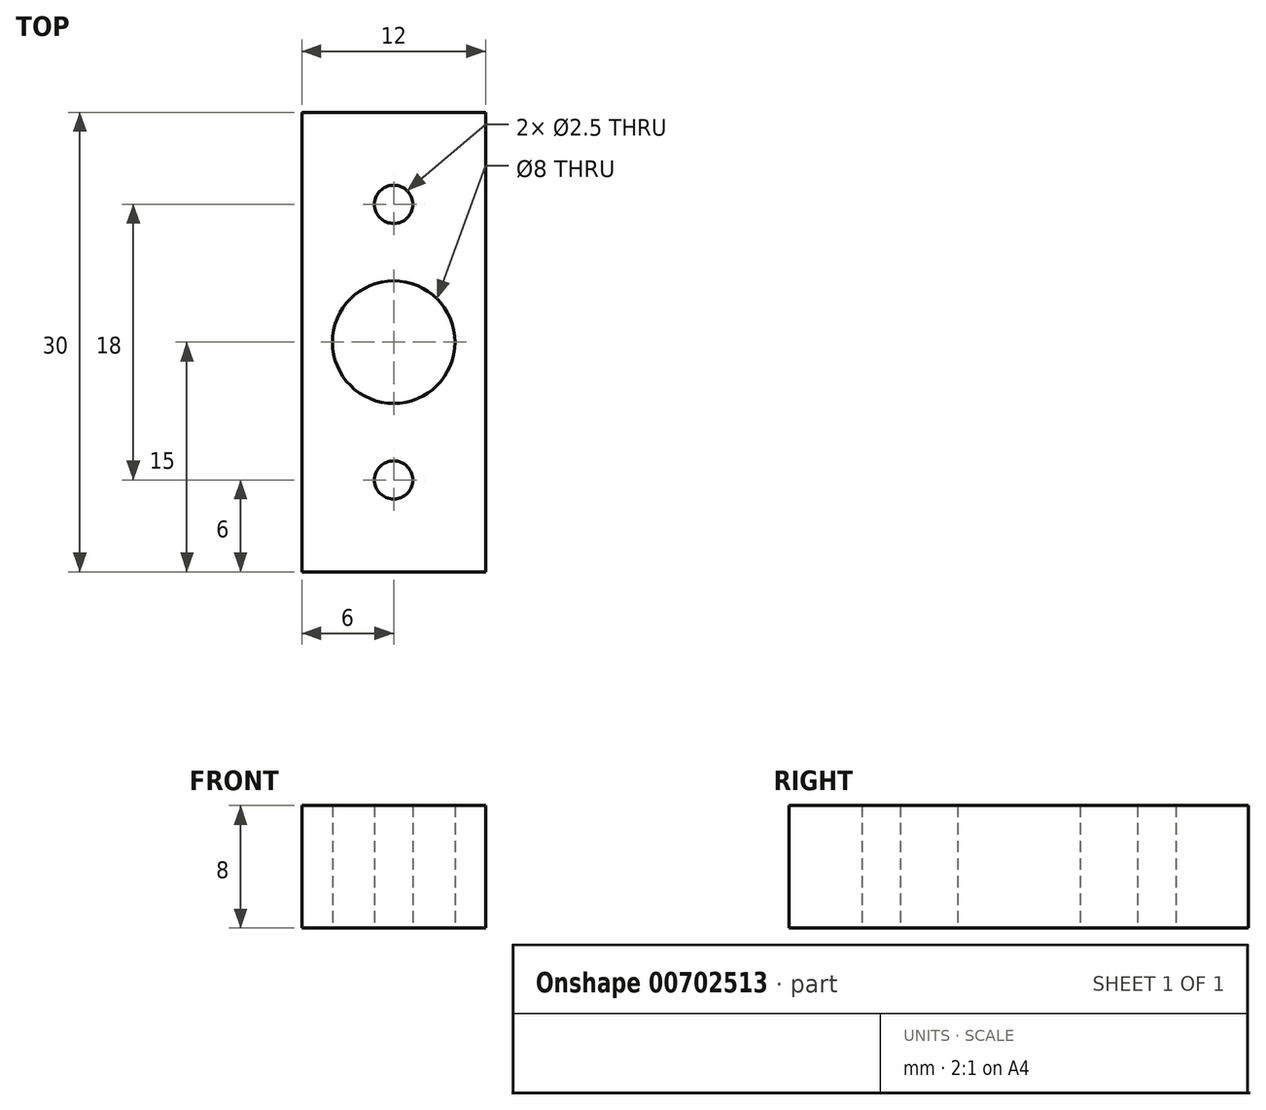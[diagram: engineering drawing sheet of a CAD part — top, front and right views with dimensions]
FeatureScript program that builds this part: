
annotation { "Feature Type Name" : "Feature", "Feature Type Description" : "" }
export const myFeature = defineFeature(function(context is Context, id is Id, definition is map)
    precondition{}
    {
        {
            var Q0;
            Q0=qCreatedBy(makeId("Top.planeOp"),FACE);
            var sketch = newSketch(context, id + "F0", { "sketchPlane" : qUnion([Q0])});
            skLineSegment(sketch, "E0.bottom", {"start": v(6, 15) * mm, "end": v(-6, 15) * mm});
            skLineSegment(sketch, "E0.top", {"start": v(6, -15) * mm, "end": v(-6, -15) * mm});
            skLineSegment(sketch, "E0.left", {"start": v(6, 15) * mm, "end": v(6, -15) * mm});
            skLineSegment(sketch, "E0.right", {"start": v(-6, 15) * mm, "end": v(-6, -15) * mm});
            skPoint(sketch, "E0.middle", {"position": v(0, 0) * mm});
            skSolve(sketch);
        }
        {
            var Q0;
            Q0 = qSketchRegion(id + "F0", true);
            extrude(context, id + "F1", {"entities" : qUnion([Q0]), "depth" : 8 * mm, "offsetDistance" : 25 * mm});
        }
        {
            var Q0;
            Q0=qCreatedBy(makeId("Top.planeOp"),FACE);
            var sketch = newSketch(context, id + "F2", { "sketchPlane" : qUnion([Q0])});
            skCircle(sketch, "E1", {"center": v(0, 0) * mm, "radius": 4 * mm});
            skSolve(sketch);
        }
        {
            var Q0;
            Q0 = qSketchRegion(id + "F2", true);
            extrude(context, id + "F3", {"entities" : qUnion([Q0]), "operationType" : NewBodyOperationType.REMOVE, "endBound" : BoundingType.THROUGH_ALL, "depth" : 25 * mm, "offsetDistance" : 25 * mm});
        }
        {
            var Q0;
            Q0=qCreatedBy(makeId("Top.planeOp"),FACE);
            var sketch = newSketch(context, id + "F4", { "sketchPlane" : qUnion([Q0])});
            skCircle(sketch, "E2", {"center": v(0, -9) * mm, "radius": 1.5 * mm, "construction": true});
            skLineSegment(sketch, "E3", {"start": v(-14.47, 0) * mm, "end": v(21.78, 0) * mm, "construction": true});
            skCircle(sketch, "E4.MirrorC", {"center": v(0, 9) * mm, "radius": 1.5 * mm, "construction": true});
            skSolve(sketch);
        }
        {
            var Q0;
            Q0=sQuery(id+"F4.wireOp",VERTEX,"E4.MirrorC.center");
            var Q1;
            Q1=sQuery(id+"F4.wireOp",VERTEX,"E2.center");
            var Q2;
            Q2=makeQuery(id+"F1.opExtrude","SWEPT_BODY",BODY,{"disambiguationData":[OSD([sQuery(id+"F0.wireOp",EDGE,"E0.bottom"),sQuery(id+"F0.wireOp",EDGE,"E0.top"),sQuery(id+"F0.wireOp",EDGE,"E0.left"),sQuery(id+"F0.wireOp",EDGE,"E0.right")])]});
            hole(context, id + "F5", {"style" : HoleStyle.SIMPLE, "endStyle" : HoleEndStyle.THROUGH, "oppositeDirection" : true, "standardTappedOrClearance" : lookupTablePath({ "standard" : "ISO", "engagement" : "75%", "pitch" : "0.5 mm", "size" : "M3", "type" : "Tapped" }), "standardBlindInLast" : lookupTablePath({ "standard" : "ISO", "engagement" : "75%", "pitch" : "0.5 mm", "size" : "M3", "type" : "Tapped" }), "holeDiameter" : 2.5 * mm, "majorDiameter" : 3 * mm, "showTappedDepth" : true, "isTappedThrough" : true, "tappedDepth" : 12 * mm, "tapClearance" : 3, "locations" : qUnion([Q0, Q1]), "scope" : qUnion([Q2])});
        }
    });
